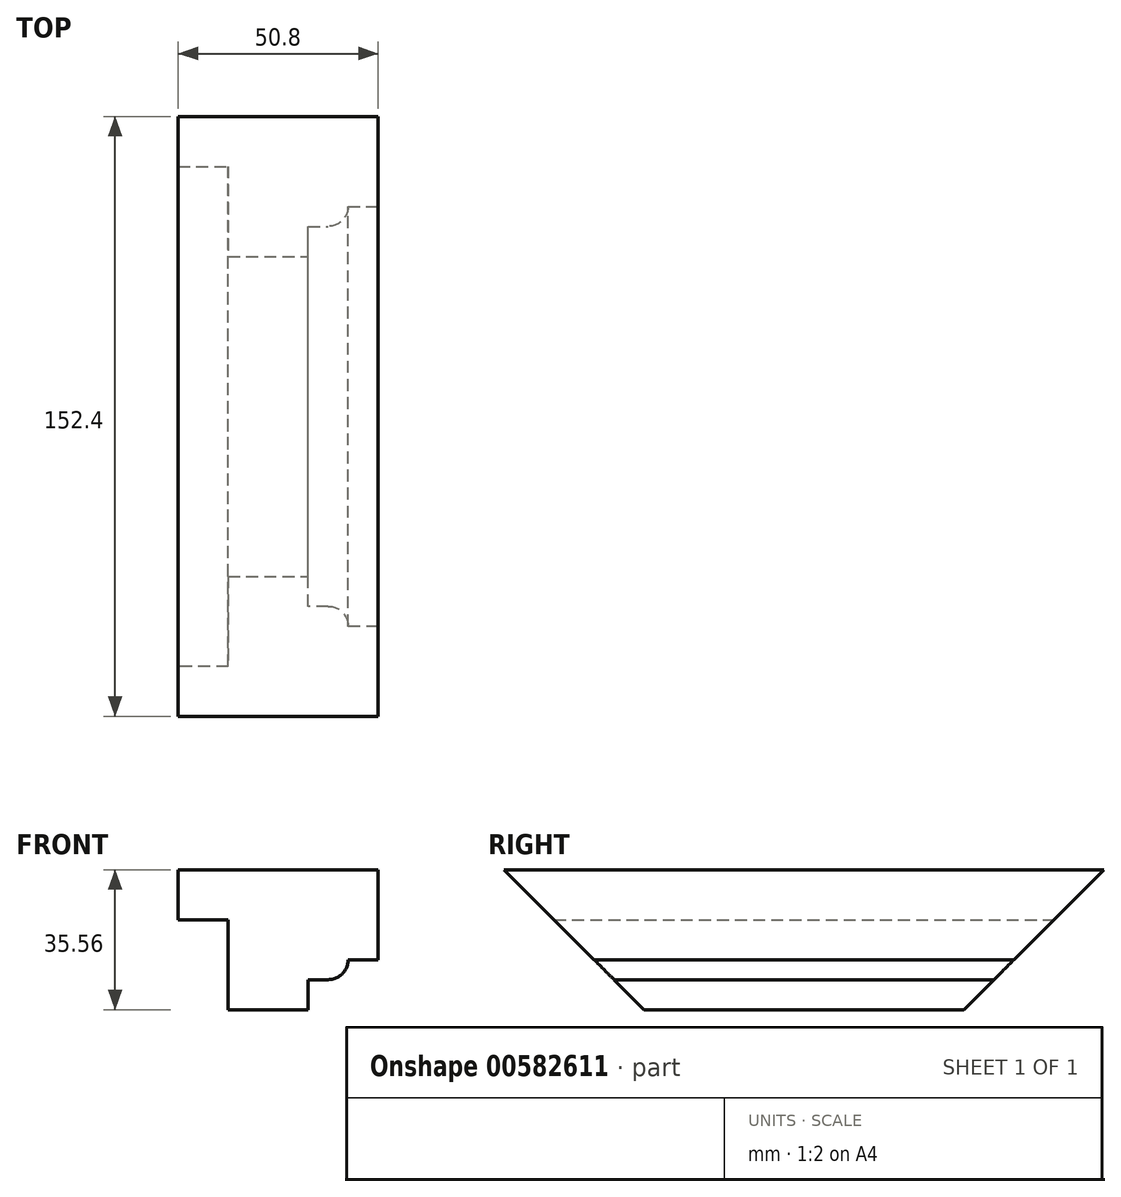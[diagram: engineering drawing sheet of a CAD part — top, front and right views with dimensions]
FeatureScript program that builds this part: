
annotation { "Feature Type Name" : "Feature", "Feature Type Description" : "" }
export const myFeature = defineFeature(function(context is Context, id is Id, definition is map)
    precondition{}
    {
        {
            var Q0;
            Q0=qCreatedBy(makeId("Front.planeOp"),FACE);
            var sketch = newSketch(context, id + "F0", { "sketchPlane" : qUnion([Q0])});
            skLineSegment(sketch, "E0", {"start": v(-25.4, 35.56) * mm, "end": v(25.4, 35.56) * mm});
            skLineSegment(sketch, "E1", {"start": v(25.4, 35.56) * mm, "end": v(25.4, 12.7) * mm});
            skLineSegment(sketch, "E2", {"start": v(25.4, 12.7) * mm, "end": v(17.78, 12.7) * mm});
            skLineSegment(sketch, "E3", {"start": v(17.78, 12.7) * mm, "end": v(17.78, 7.62) * mm});
            skLineSegment(sketch, "E4", {"start": v(17.78, 7.62) * mm, "end": v(7.62, 7.62) * mm});
            skLineSegment(sketch, "E5", {"start": v(7.62, 7.62) * mm, "end": v(7.62, 0) * mm});
            skLineSegment(sketch, "E6", {"start": v(7.62, 0) * mm, "end": v(0, 0) * mm});
            skLineSegment(sketch, "E7", {"start": v(0, 0) * mm, "end": v(-12.7, 0) * mm});
            skLineSegment(sketch, "E8", {"start": v(-12.7, 0) * mm, "end": v(-12.7, 22.86) * mm});
            skLineSegment(sketch, "E9", {"start": v(-12.7, 22.86) * mm, "end": v(-25.4, 22.86) * mm});
            skLineSegment(sketch, "E10", {"start": v(-25.4, 22.86) * mm, "end": v(-25.4, 35.56) * mm});
            skSolve(sketch);
        }
        {
            var Q0;
            Q0 = qSketchRegion(id + "F0", true);
            extrude(context, id + "F1", {"entities" : qUnion([Q0]), "depth" : 152.4 * mm, "offsetDistance" : 25.4 * mm});
        }
        {
            var Q0;
            Q0=makeQuery(id+"F1.opExtrude","SWEPT_FACE",FACE,{"disambiguationData":[OSD([sQuery(id+"F0.wireOp",EDGE,"E1")])]});
            var sketch = newSketch(context, id + "F2", { "sketchPlane" : qUnion([Q0])});
            skLineSegment(sketch, "E11", {"start": v(-152.4, 35.56) * mm, "end": v(-116.84, 0) * mm});
            skLineSegment(sketch, "E12", {"start": v(-116.84, 0) * mm, "end": v(-152.4, 0) * mm});
            skLineSegment(sketch, "E13", {"start": v(-152.4, 0) * mm, "end": v(-152.4, 35.56) * mm});
            skSolve(sketch);
        }
        {
            var Q0;
            Q0 = qSketchRegion(id + "F2", true);
            extrude(context, id + "F3", {"entities" : qUnion([Q0]), "operationType" : NewBodyOperationType.REMOVE, "oppositeDirection" : true, "depth" : 50.8 * mm, "offsetDistance" : 25.4 * mm});
        }
        {
            var Q0;
            Q0=makeQuery(id+"F1.opExtrude","SWEPT_FACE",FACE,{"disambiguationData":[OSD([sQuery(id+"F0.wireOp",EDGE,"E1")])]});
            var sketch = newSketch(context, id + "F4", { "sketchPlane" : qUnion([Q0])});
            skLineSegment(sketch, "E14", {"start": v(0, 35.56) * mm, "end": v(0, 0) * mm});
            skLineSegment(sketch, "E15", {"start": v(0, 0) * mm, "end": v(-35.56, 0) * mm});
            skLineSegment(sketch, "E16", {"start": v(-35.56, 0) * mm, "end": v(0, 35.56) * mm});
            skSolve(sketch);
        }
        {
            var Q0;
            Q0 = qSketchRegion(id + "F4", true);
            extrude(context, id + "F5", {"entities" : qUnion([Q0]), "operationType" : NewBodyOperationType.REMOVE, "oppositeDirection" : true, "depth" : 50.8 * mm, "offsetDistance" : 25.4 * mm});
        }
        {
            var Q0;
            Q0=makeQuery(id+"F1.opExtrude","SWEPT_EDGE",EDGE,{"disambiguationData":[OSD([sQuery(id+"F0.wireOp",EDGE,"E3"),sQuery(id+"F0.wireOp",EDGE,"E4")])]});
            fillet(context, id + "F6", {"entities" : qUnion([Q0]), "radius" : 5.08 * mm, "tangentPropagation" : true, "allowEdgeOverflow" : false});
        }
    });
